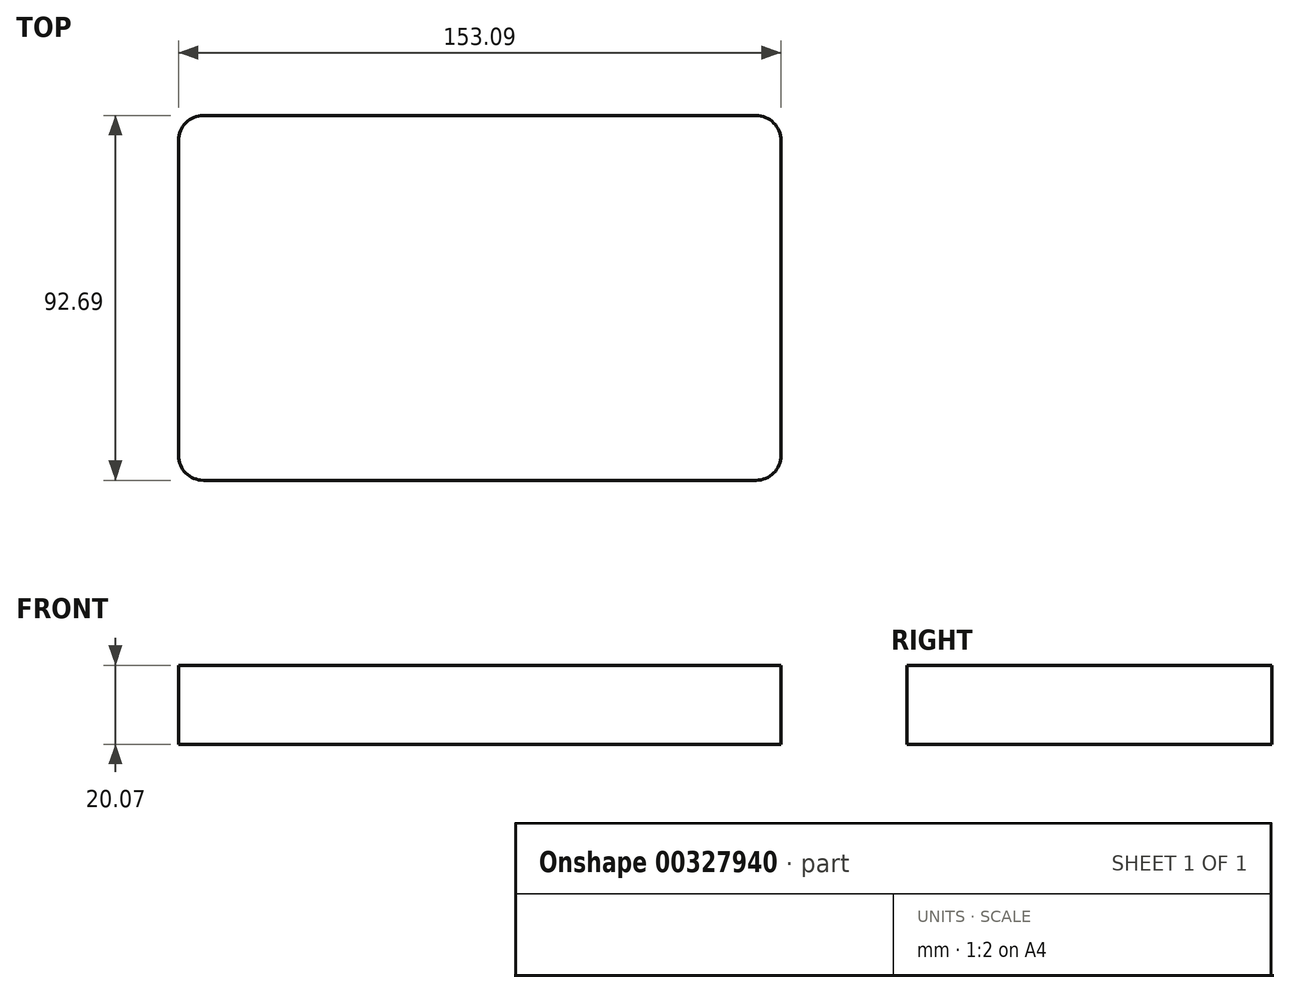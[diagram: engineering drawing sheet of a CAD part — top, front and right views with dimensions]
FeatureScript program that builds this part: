
annotation { "Feature Type Name" : "Feature", "Feature Type Description" : "" }
export const myFeature = defineFeature(function(context is Context, id is Id, definition is map)
    precondition{}
    {
        {
            var Q0;
            Q0=qCreatedBy(makeId("Top.planeOp"),FACE);
            var sketch = newSketch(context, id + "F0", { "sketchPlane" : qUnion([Q0])});
            skLineSegment(sketch, "E0.bottom", {"start": v(-70.59, -74.55) * mm, "end": v(69.8, -74.55) * mm});
            skLineSegment(sketch, "E0.top", {"start": v(-70.59, 18.14) * mm, "end": v(69.8, 18.14) * mm});
            skLineSegment(sketch, "E0.left", {"start": v(-76.94, -68.2) * mm, "end": v(-76.94, 11.79) * mm});
            skLineSegment(sketch, "E0.right", {"start": v(76.15, -68.2) * mm, "end": v(76.15, 11.79) * mm});
            skPoint(sketch, "E1.visualSharp", {"position": v(-76.94, 18.14) * mm});
            skArc(sketch, "E1.filletArc", {"start": v(-70.59, 18.14) * mm, "mid": v(-75.08, 16.28) * mm, "end": v(-76.94, 11.79) * mm});
            skPoint(sketch, "E2.visualSharp", {"position": v(-76.94, -74.55) * mm});
            skArc(sketch, "E2.filletArc", {"start": v(-76.94, -68.2) * mm, "mid": v(-75.08, -72.69) * mm, "end": v(-70.59, -74.55) * mm});
            skPoint(sketch, "E3.visualSharp", {"position": v(76.15, -74.55) * mm});
            skArc(sketch, "E3.filletArc", {"start": v(69.8, -74.55) * mm, "mid": v(74.29, -72.69) * mm, "end": v(76.15, -68.2) * mm});
            skPoint(sketch, "E4.visualSharp", {"position": v(76.15, 18.14) * mm});
            skArc(sketch, "E4.filletArc", {"start": v(76.15, 11.79) * mm, "mid": v(74.29, 16.28) * mm, "end": v(69.8, 18.14) * mm});
            skSolve(sketch);
        }
        {
            var Q0;
            Q0=makeQuery(id+"F0.imprint","IMPRINT",FACE,{"disambiguationData":[TD([[makeQuery(id+"F0.imprint","IMPRINT",EDGE,{"derivedFrom":sQuery(id+"F0.wireOp",EDGE,"E0.bottom")}),1.0]])]});
            extrude(context, id + "F1", {"entities" : qUnion([Q0]), "depth" : 20.07 * mm});
        }
    });
